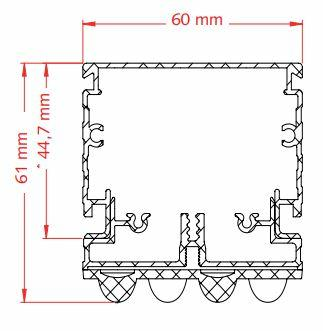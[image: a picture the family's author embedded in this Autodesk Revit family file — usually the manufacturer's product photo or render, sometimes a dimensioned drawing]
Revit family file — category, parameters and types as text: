
# Revit family: Rowan 1030mm
name_source: partatom
category: Lighting Fixtures
revit_build: Autodesk Revit 2017 (Build: 20190508_0315(x64)
units: mm (PartAtom-declared; Revit-internal decimal feet)

## family parameters
Always vertical = No
Cut with Voids When Loaded = No
Light Source = No
Part Type = Normal
Room Calculation Point = No
Round Connector Dimension = Use Diameter
Shared = No
Work Plane-Based = No

## types (3) — shared parameters
Article Number = On Request
Assembly Code = 63.0
Description = Veko Lightline
IK Value = IK02
IP Value = IP20
IfcExportAs = IfcLightFixtureType
IfcExportType = POINTSOURCE
Lamp = LED
Manufacturer = Veko Lightsystems
URL = https://www.veko.com
Wattage Comments = Load can vary between 10,3 - 154,5(W)

## per-type parameters (varying)
| type | Apparent Load | Model | Selected Optic |
| Narrow | 10 VA | Rowan Narrow | Optics Rowan 1030mm : Narrow |
| Semi Wide | 11 VA | Rowan Semi Wide | Optics Rowan 1030mm : Semi Wide |
| Wide | 11 VA | Rowan Wide | Optics Rowan 1030mm : Wide |

## geometry (parser evidence)
native form markers: Sweep x52
no freeform markers — native parametric forms only
